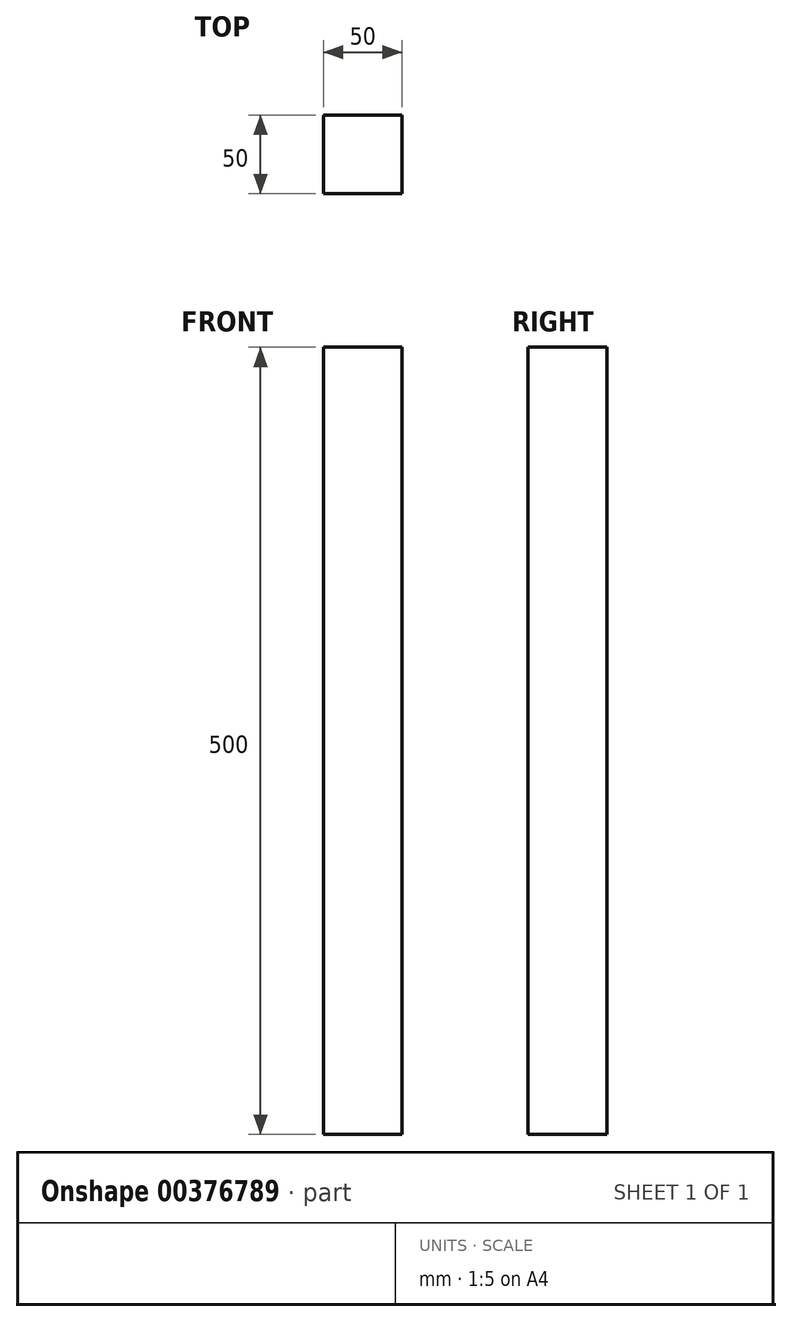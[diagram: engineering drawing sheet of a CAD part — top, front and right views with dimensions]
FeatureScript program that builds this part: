
annotation { "Feature Type Name" : "Feature", "Feature Type Description" : "" }
export const myFeature = defineFeature(function(context is Context, id is Id, definition is map)
    precondition{}
    {
        {
            var Q0;
            Q0=qCreatedBy(makeId("Top.planeOp"),FACE);
            var sketch = newSketch(context, id + "F0", { "sketchPlane" : qUnion([Q0])});
            skLineSegment(sketch, "E0.bottom", {"start": v(0, 0) * mm, "end": v(-50, 0) * mm});
            skLineSegment(sketch, "E0.top", {"start": v(0, 50) * mm, "end": v(-50, 50) * mm});
            skLineSegment(sketch, "E0.left", {"start": v(0, 0) * mm, "end": v(0, 50) * mm});
            skLineSegment(sketch, "E0.right", {"start": v(-50, 0) * mm, "end": v(-50, 50) * mm});
            skSolve(sketch);
        }
        {
            var Q0;
            Q0=qSketchRegion(id+"F0",true);
            extrude(context, id + "F1", {"entities" : qUnion([Q0]), "depth" : 500 * mm});
        }
    });
